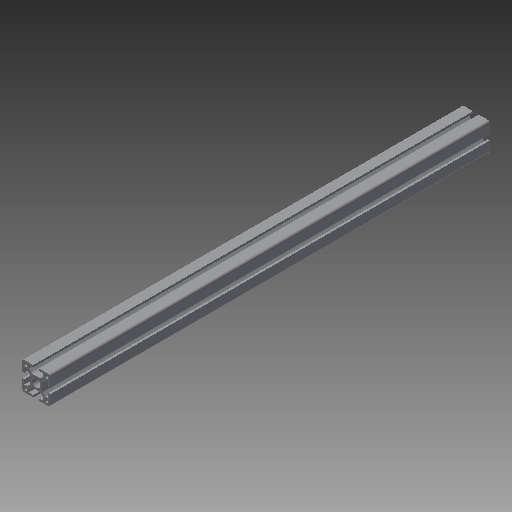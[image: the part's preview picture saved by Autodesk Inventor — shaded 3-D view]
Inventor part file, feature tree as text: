
AUTODESK INVENTOR PART (.ipt)
format: ipt  version: 2018 (Build 220112000, 112)  size: 223,232 bytes
history: native  units: mm
features: other x42, sketch x5, hole x4, extrude x1
ambient origin geometry x8: Origin, YZ Plane, XZ Plane, XY Plane, X Axis, Y Axis, Z Axis, Center Point
bodies: Solid1 (feature_tree)
feature tree (52):
  extrude  "Extrusion1"  [1 undecoded]
  hole  "Drilling 1"  [1 undecoded]
  hole  "Drilling 2"  [1 undecoded]
  hole  "Drilling 3"  [1 undecoded]
  hole  "Drilling 4"  [1 undecoded]
  other  "side_4d_XY"
  other  "side_4d_YZ"
  other  "side_4d_ZX"
  other  "side_4d_X"
  other  "side_4d_Y"
  other  "side_4d_Z"
  other  "side_4d_Center"
  other  "side_1a_XY"
  other  "side_1a_YZ"
  other  "side_1a_ZX"
  other  "side_1a_X"
  other  "side_1a_Y"
  other  "side_1a_Z"
  other  "side_1a_Center"
  other  "side_2b_XY"
  other  "side_2b_YZ"
  other  "side_2b_ZX"
  other  "side_2b_X"
  other  "side_2b_Y"
  other  "side_2b_Z"
  other  "side_2b_Center"
  other  "side_3c_XY"
  other  "side_3c_YZ"
  other  "side_3c_ZX"
  other  "side_3c_X"
  other  "side_3c_Y"
  other  "side_3c_Z"
  other  "side_3c_Center"
  other  "end_XY"
  other  "end_YZ"
  other  "end_ZX"
  other  "end_X"
  other  "end_Y"
  other  "end_Z"
  other  "end_Center"
  other  "start_XY"
  other  "start_YZ"
  other  "start_ZX"
  other  "start_X"
  other  "start_Y"
  other  "start_Z"
  other  "start_Center"
  sketch  "Skizze_1"  dims[d0=627.0mm d1=0.0mm]
  sketch  "Sketch2"  dims[d2=5.0mm d3=6.0mm d4=4.0mm d5=2.0mm d6=90.0deg d7=6000.0mm d8=0.0mm]
  sketch  "Sketch3"  dims[d9=5.0mm d10=6.0mm d11=4.0mm d12=2.0mm d13=90.0deg d14=6000.0mm d15=0.0mm]
  sketch  "Sketch4"  dims[d16=5.0mm d17=6.0mm d18=4.0mm d19=2.0mm d20=90.0deg d21=6000.0mm d22=0.0mm]
  sketch  "Sketch5"  dims[d23=5.0mm d24=6.0mm d25=4.0mm d26=2.0mm d27=90.0deg d28=6000.0mm d29=0.0mm]
note: 5 required parameter values undecoded (feature->parameter linkage not recoverable at this tier; creation-order binding heuristic only, values carry confidence <= 0.55)
